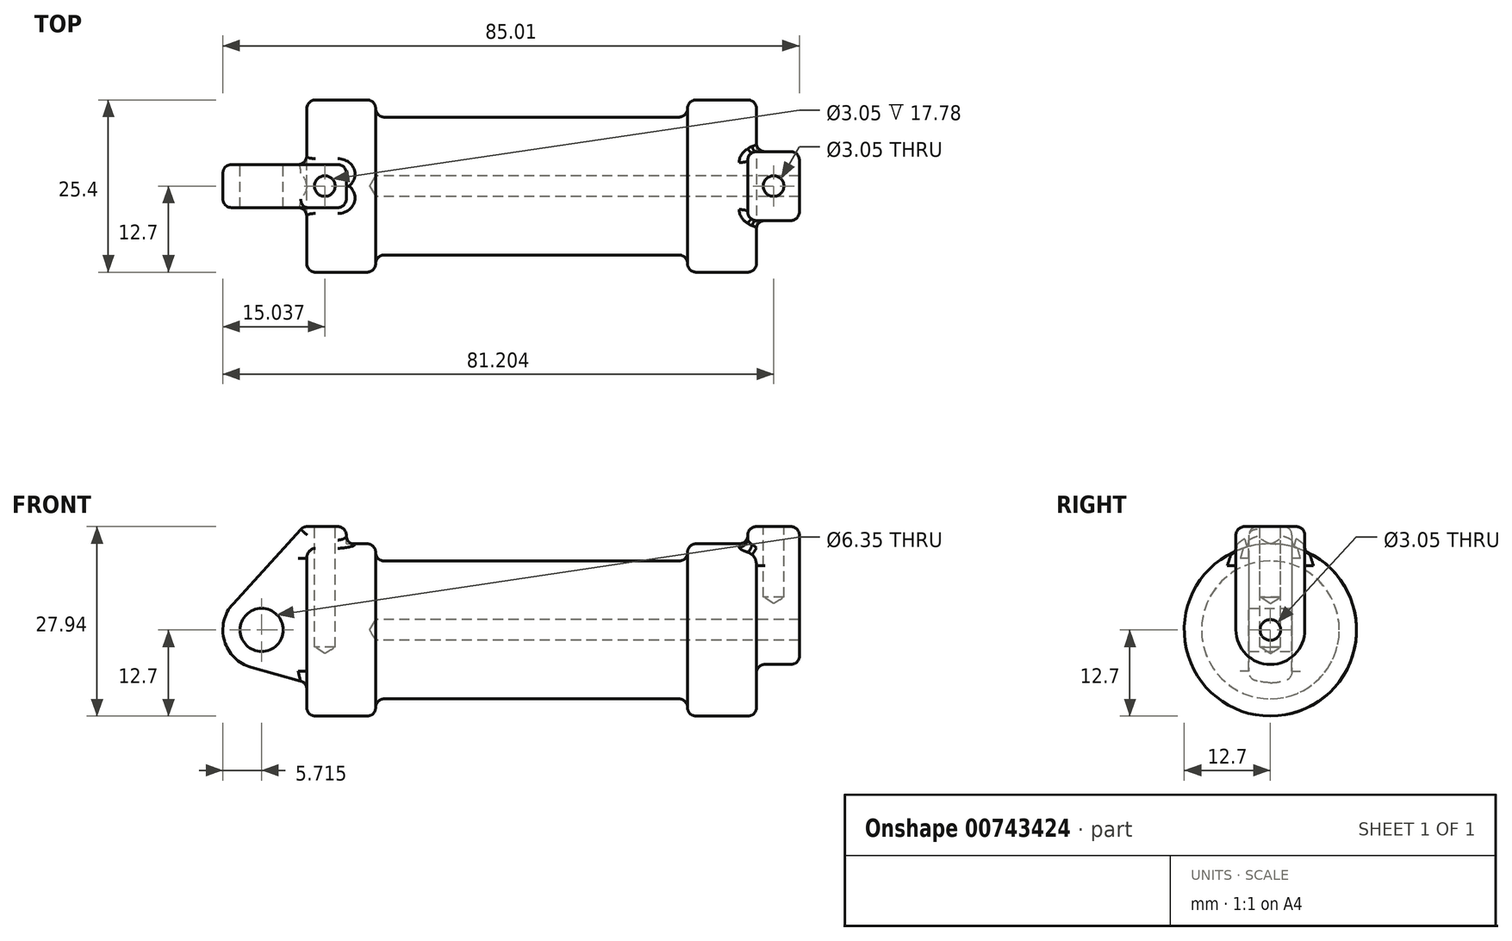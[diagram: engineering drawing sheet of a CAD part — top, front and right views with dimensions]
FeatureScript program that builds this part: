
annotation { "Feature Type Name" : "Feature", "Feature Type Description" : "" }
export const myFeature = defineFeature(function(context is Context, id is Id, definition is map)
    precondition{}
    {
        {
            var Q0;
            Q0=qCreatedBy(makeId("Front.planeOp"),FACE);
            var sketch = newSketch(context, id + "F0", { "sketchPlane" : qUnion([Q0])});
            skLineSegment(sketch, "E0", {"start": v(0, 0) * mm, "end": v(0, 12.7) * mm});
            skLineSegment(sketch, "E1", {"start": v(0, 12.7) * mm, "end": v(10.16, 12.7) * mm});
            skLineSegment(sketch, "E2", {"start": v(10.16, 12.7) * mm, "end": v(10.16, 10.16) * mm});
            skLineSegment(sketch, "E3", {"start": v(10.16, 10.16) * mm, "end": v(56.13, 10.16) * mm});
            skLineSegment(sketch, "E4", {"start": v(56.13, 10.16) * mm, "end": v(56.13, 12.7) * mm});
            skLineSegment(sketch, "E5", {"start": v(56.13, 12.7) * mm, "end": v(66.3, 12.7) * mm});
            skLineSegment(sketch, "E6", {"start": v(66.3, 12.7) * mm, "end": v(66.3, 0) * mm});
            skLineSegment(sketch, "E7", {"start": v(66.3, 0) * mm, "end": v(0, 0) * mm});
            skLineSegment(sketch, "E8", {"start": v(5.84, 15.24) * mm, "end": v(-0.5, 15.24) * mm});
            skLineSegment(sketch, "E9", {"start": v(-0.5, 15.24) * mm, "end": v(-10.88, 3.85) * mm});
            skLineSegment(sketch, "E10", {"start": v(0, 0) * mm, "end": v(-6.65, 0) * mm});
            skCircle(sketch, "E11", {"center": v(-6.65, 0) * mm, "radius": 5.72 * mm});
            skCircle(sketch, "E12", {"center": v(-6.65, 0) * mm, "radius": 3.18 * mm});
            skLineSegment(sketch, "E13", {"start": v(5.84, 15.24) * mm, "end": v(5.84, -9.4) * mm});
            skLineSegment(sketch, "E14", {"start": v(5.84, -9.4) * mm, "end": v(-8.18, -5.5) * mm});
            skSolve(sketch);
        }
        {
            var Q0;
            {var subQ0=sQuery(id+"F0.wireOp",EDGE,"E0");Q0=makeQuery(id+"F0.imprint","IMPRINT",FACE,{"disambiguationData":[TD([[makeQuery(id+"F0.imprint","IMPRINT",EDGE,{"derivedFrom":subQ0}),-1.0]])]});}
            var Q1;
            {var subQ0=sQuery(id+"F0.wireOp",EDGE,"E2");Q1=makeQuery(id+"F0.imprint","IMPRINT",FACE,{"disambiguationData":[TD([[makeQuery(id+"F0.imprint","IMPRINT",EDGE,{"derivedFrom":subQ0}),-1.0]])]});}
            var Q2;
            Q2=sQuery(id+"F0.wireOp",EDGE,"E7");
            revolve(context, id + "F1", {"surfaceOperationType" : NewSurfaceOperationType.NEW, "entities" : qUnion([Q0, Q1]), "axis" : qUnion([Q2]), "revolveType" : RevolveType.FULL});
        }
        {
            var Q0;
            {var subQ0=sQuery(id+"F0.wireOp",EDGE,"E14");Q0=makeQuery(id+"F0.imprint","IMPRINT",FACE,{"disambiguationData":[TD([[makeQuery(id+"F0.imprint","IMPRINT",EDGE,{"derivedFrom":subQ0}),-1.0]])]});}
            var Q1;
            {var subQ5=sQuery(id+"F0.wireOp",EDGE,"E12");Q1=makeQuery(id+"F0.imprint","IMPRINT",FACE,{"disambiguationData":[TD([[makeQuery(id+"F0.imprint","IMPRINT",EDGE,{"derivedFrom":subQ5}),-1.0]])]});}
            var Q2;
            {var subQ1=sQuery(id+"F0.wireOp",EDGE,"E0");Q2=makeQuery(id+"F0.imprint","IMPRINT",FACE,{"disambiguationData":[TD([[makeQuery(id+"F0.imprint","IMPRINT",EDGE,{"derivedFrom":subQ1}),1.0]])]});}
            var Q3;
            {var subQ0=sQuery(id+"F0.wireOp",EDGE,"E0");Q3=makeQuery(id+"F0.imprint","IMPRINT",FACE,{"disambiguationData":[TD([[makeQuery(id+"F0.imprint","IMPRINT",EDGE,{"derivedFrom":subQ0}),-1.0]])]});}
            extrude(context, id + "F2", {"entities" : qUnion([Q0, Q1, Q2, Q3]), "operationType" : NewBodyOperationType.ADD, "endBound" : BoundingType.SYMMETRIC, "depth" : 6.35 * mm, "offsetDistance" : 25.4 * mm});
        }
        {
            var Q0;
            Q0=makeQuery(id+"F1.opRevolve","SWEPT_FACE",FACE,{"disambiguationData":[OSD([sQuery(id+"F0.wireOp",EDGE,"E6")])]});
            var sketch = newSketch(context, id + "F3", { "sketchPlane" : qUnion([Q0])});
            skCircle(sketch, "E15", {"center": v(0, 0) * mm, "radius": 1.52 * mm});
            skCircle(sketch, "E16", {"center": v(0, 0) * mm, "radius": 5.08 * mm});
            skLineSegment(sketch, "E17", {"start": v(5.08, 0) * mm, "end": v(5.08, 15.24) * mm});
            skLineSegment(sketch, "E18", {"start": v(5.08, 15.24) * mm, "end": v(-5.08, 15.24) * mm});
            skLineSegment(sketch, "E19", {"start": v(-5.08, 15.24) * mm, "end": v(-5.08, 0) * mm});
            skSolve(sketch);
        }
        {
            var Q0;
            {var subQ0=sQuery(id+"F3.wireOp",EDGE,"E18");Q0=makeQuery(id+"F3.imprint","IMPRINT",FACE,{"disambiguationData":[TD([[makeQuery(id+"F3.imprint","IMPRINT",EDGE,{"derivedFrom":subQ0}),1.0]])]});}
            var Q1;
            {var subQ0=sQuery(id+"F3.wireOp",EDGE,"E17");var subQ1=sQuery(id+"F3.wireOp",EDGE,"E16");var subQ2=makeQuery(id+"F3.imprint","INTERSECT",VERTEX,{"derivedFrom":[subQ1,subQ0]});Q1=makeQuery(id+"F3.imprint","IMPRINT",FACE,{"disambiguationData":[TD([[makeQuery(id+"F3.imprint","IMPRINT",EDGE,{"disambiguationData":[TD([[subQ2,-1.0]])],"derivedFrom":subQ1}),-1.0]])]});}
            var Q2;
            Q2=makeQuery(id+"F3.imprint","IMPRINT",FACE,{"disambiguationData":[TD([[makeQuery(id+"F3.imprint","IMPRINT",EDGE,{"derivedFrom":sQuery(id+"F3.wireOp",EDGE,"E15")}),-1.0]])]});
            extrude(context, id + "F4", {"entities" : qUnion([Q0, Q1, Q2]), "operationType" : NewBodyOperationType.ADD, "depth" : 6.35 * mm, "offsetDistance" : 25.4 * mm, "hasSecondDirection" : true, "secondDirectionOppositeDirection" : true, "secondDirectionDepth" : 1.27 * mm});
        }
        {
            var Q0;
            Q0=sQuery(id+"F3.wireOp",VERTEX,"E15.center");
            var Q1;
            Q1=makeQuery(id+"F1.opRevolve","SWEPT_BODY",BODY,{"disambiguationData":[OSD([sQuery(id+"F0.wireOp",EDGE,"E0"),sQuery(id+"F0.wireOp",EDGE,"E1"),sQuery(id+"F0.wireOp",EDGE,"E2"),sQuery(id+"F0.wireOp",EDGE,"E3"),sQuery(id+"F0.wireOp",EDGE,"E4"),sQuery(id+"F0.wireOp",EDGE,"E5"),sQuery(id+"F0.wireOp",EDGE,"E6"),sQuery(id+"F0.wireOp",EDGE,"E7")])]});
            hole(context, id + "F5", {"style" : HoleStyle.SIMPLE, "endStyle" : HoleEndStyle.BLIND, "holeDiameter" : 3.05 * mm, "majorDiameter" : 6.35 * mm, "holeDepth" : 56.13 * mm, "isTappedThrough" : true, "tappedDepth" : 12.7 * mm, "tapClearance" : 3, "locations" : qUnion([Q0]), "scope" : qUnion([Q1])});
        }
        {
            var Q0;
            Q0=makeQuery(id+"F2.opExtrude","SWEPT_FACE",FACE,{"disambiguationData":[OSD([sQuery(id+"F0.wireOp",EDGE,"E8")])]});
            var sketch = newSketch(context, id + "F6", { "sketchPlane" : qUnion([Q0])});
            skLineSegment(sketch, "E20.0.0", {"start": v(65.02, 5.08) * mm, "end": v(65.02, -5.08) * mm});
            skLineSegment(sketch, "E20.0.1", {"start": v(65.02, -5.08) * mm, "end": v(72.64, -5.08) * mm});
            skLineSegment(sketch, "E20.0.2", {"start": v(72.64, -5.08) * mm, "end": v(72.64, 5.08) * mm});
            skLineSegment(sketch, "E20.0.3", {"start": v(72.64, 5.08) * mm, "end": v(65.02, 5.08) * mm});
            skLineSegment(sketch, "E21", {"start": v(-0.5, 0) * mm, "end": v(72.64, 0) * mm, "construction": true});
            skLineSegment(sketch, "E22", {"start": v(2.67, 3.18) * mm, "end": v(2.67, -3.18) * mm, "construction": true});
            skLineSegment(sketch, "E23", {"start": v(68.83, 5.08) * mm, "end": v(68.83, -5.08) * mm, "construction": true});
            skCircle(sketch, "E24", {"center": v(2.67, 0) * mm, "radius": 1.52 * mm});
            skCircle(sketch, "E25", {"center": v(68.83, 0) * mm, "radius": 1.52 * mm});
            skSolve(sketch);
        }
        {
            var Q0;
            Q0=sQuery(id+"F6.wireOp",VERTEX,"E24.center");
            var Q1;
            Q1=makeQuery(id+"F1.opRevolve","SWEPT_BODY",BODY,{"disambiguationData":[OSD([sQuery(id+"F0.wireOp",EDGE,"E0"),sQuery(id+"F0.wireOp",EDGE,"E1"),sQuery(id+"F0.wireOp",EDGE,"E2"),sQuery(id+"F0.wireOp",EDGE,"E3"),sQuery(id+"F0.wireOp",EDGE,"E4"),sQuery(id+"F0.wireOp",EDGE,"E5"),sQuery(id+"F0.wireOp",EDGE,"E6"),sQuery(id+"F0.wireOp",EDGE,"E7")])]});
            hole(context, id + "F7", {"style" : HoleStyle.SIMPLE, "endStyle" : HoleEndStyle.BLIND, "holeDiameter" : 3.05 * mm, "majorDiameter" : 6.35 * mm, "holeDepth" : 17.78 * mm, "isTappedThrough" : true, "tappedDepth" : 12.7 * mm, "tapClearance" : 3, "locations" : qUnion([Q0]), "scope" : qUnion([Q1])});
        }
        {
            var Q0;
            Q0=sQuery(id+"F6.wireOp",VERTEX,"E25.center");
            var Q1;
            Q1=makeQuery(id+"F1.opRevolve","SWEPT_BODY",BODY,{"disambiguationData":[OSD([sQuery(id+"F0.wireOp",EDGE,"E0"),sQuery(id+"F0.wireOp",EDGE,"E1"),sQuery(id+"F0.wireOp",EDGE,"E2"),sQuery(id+"F0.wireOp",EDGE,"E3"),sQuery(id+"F0.wireOp",EDGE,"E4"),sQuery(id+"F0.wireOp",EDGE,"E5"),sQuery(id+"F0.wireOp",EDGE,"E6"),sQuery(id+"F0.wireOp",EDGE,"E7")])]});
            hole(context, id + "F8", {"style" : HoleStyle.SIMPLE, "endStyle" : HoleEndStyle.BLIND, "holeDiameter" : 3.05 * mm, "majorDiameter" : 6.35 * mm, "holeDepth" : 10.4 * mm, "isTappedThrough" : true, "tappedDepth" : 12.7 * mm, "tapClearance" : 3, "locations" : qUnion([Q0]), "scope" : qUnion([Q1])});
        }
        {
            var Q0;
            Q0=makeQuery(id+"F1.opRevolve","SWEPT_EDGE",EDGE,{"disambiguationData":[OSD([sQuery(id+"F0.wireOp",EDGE,"E0"),sQuery(id+"F0.wireOp",EDGE,"E1")])]});
            var Q1;
            Q1=makeQuery(id+"F1.opRevolve","SWEPT_EDGE",EDGE,{"disambiguationData":[OSD([sQuery(id+"F0.wireOp",EDGE,"E1"),sQuery(id+"F0.wireOp",EDGE,"E2")])]});
            var Q2;
            Q2=makeQuery(id+"F1.opRevolve","SWEPT_EDGE",EDGE,{"disambiguationData":[OSD([sQuery(id+"F0.wireOp",EDGE,"E2"),sQuery(id+"F0.wireOp",EDGE,"E3")])]});
            var Q3;
            Q3=makeQuery(id+"F1.opRevolve","SWEPT_EDGE",EDGE,{"disambiguationData":[OSD([sQuery(id+"F0.wireOp",EDGE,"E4"),sQuery(id+"F0.wireOp",EDGE,"E5")])]});
            var Q4;
            Q4=makeQuery(id+"F1.opRevolve","SWEPT_EDGE",EDGE,{"disambiguationData":[OSD([sQuery(id+"F0.wireOp",EDGE,"E5"),sQuery(id+"F0.wireOp",EDGE,"E6")])]});
            var Q5;
            Q5=makeQuery(id+"F1.opRevolve","SWEPT_EDGE",EDGE,{"disambiguationData":[OSD([sQuery(id+"F0.wireOp",EDGE,"E3"),sQuery(id+"F0.wireOp",EDGE,"E4")])]});
            fillet(context, id + "F9", {"entities" : qUnion([Q0, Q1, Q2, Q3, Q4, Q5]), "radius" : 1.27 * mm, "tangentPropagation" : true, "allowEdgeOverflow" : false});
        }
        {
            var Q0;
            Q0=makeQuery(id+"F2.opExtrude","SWEPT_EDGE",EDGE,{"disambiguationData":[OSD([sQuery(id+"F0.wireOp",EDGE,"E8"),sQuery(id+"F0.wireOp",EDGE,"E13")])]});
            var Q1;
            Q1=makeQuery(id+"F2.opExtrude","CAP_EDGE",EDGE,{"disambiguationData":[OSD([sQuery(id+"F0.wireOp",EDGE,"E8")])],"isStart":false});
            var Q2;
            Q2=makeQuery(id+"F2.opExtrude","CAP_EDGE",EDGE,{"disambiguationData":[OSD([sQuery(id+"F0.wireOp",EDGE,"E9")])],"isStart":false});
            var Q3;
            Q3=makeQuery(id+"F2.boolean.opBoolean","INTERSECT",EDGE,{"derivedFrom":[makeQuery(id+"F1.opRevolve","SWEPT_FACE",FACE,{"disambiguationData":[OSD([sQuery(id+"F0.wireOp",EDGE,"E0")])]}),makeQuery(id+"F2.opExtrude","CAP_FACE",FACE,{"disambiguationData":[OSD([sQuery(id+"F0.wireOp",EDGE,"E8"),sQuery(id+"F0.wireOp",EDGE,"E9"),sQuery(id+"F0.wireOp",EDGE,"E11"),sQuery(id+"F0.wireOp",EDGE,"E12"),sQuery(id+"F0.wireOp",EDGE,"E13"),sQuery(id+"F0.wireOp",EDGE,"E14")])],"isStart":false})]});
            var Q4;
            Q4=makeQuery(id+"F2.opExtrude","CAP_EDGE",EDGE,{"disambiguationData":[OSD([sQuery(id+"F0.wireOp",EDGE,"E13")])],"isStart":false});
            fillet(context, id + "F10", {"entities" : qUnion([Q0, Q1, Q2, Q3, Q4]), "radius" : 1.27 * mm, "tangentPropagation" : true, "allowEdgeOverflow" : false});
        }
        {
            var Q0;
            Q0=makeQuery(id+"F2.opExtrude","CAP_EDGE",EDGE,{"disambiguationData":[OSD([sQuery(id+"F0.wireOp",EDGE,"E11")])],"isStart":true});
            var Q1;
            Q1=makeQuery(id+"F2.opExtrude","SWEPT_EDGE",EDGE,{"disambiguationData":[OSD([sQuery(id+"F0.wireOp",EDGE,"E8"),sQuery(id+"F0.wireOp",EDGE,"E9")])]});
            var Q2;
            Q2=makeQuery(id+"F2.boolean.opBoolean","INTERSECT",EDGE,{"derivedFrom":[makeQuery(id+"F1.opRevolve","SWEPT_FACE",FACE,{"disambiguationData":[OSD([sQuery(id+"F0.wireOp",EDGE,"E0")])]}),makeQuery(id+"F2.opExtrude","CAP_FACE",FACE,{"disambiguationData":[OSD([sQuery(id+"F0.wireOp",EDGE,"E8"),sQuery(id+"F0.wireOp",EDGE,"E9"),sQuery(id+"F0.wireOp",EDGE,"E11"),sQuery(id+"F0.wireOp",EDGE,"E12"),sQuery(id+"F0.wireOp",EDGE,"E13"),sQuery(id+"F0.wireOp",EDGE,"E14")])],"isStart":true})]});
            var Q3;
            Q3=makeQuery(id+"F2.opExtrude","CAP_EDGE",EDGE,{"disambiguationData":[OSD([sQuery(id+"F0.wireOp",EDGE,"E13")])],"isStart":true});
            fillet(context, id + "F11", {"entities" : qUnion([Q0, Q1, Q2, Q3]), "radius" : 1.27 * mm, "tangentPropagation" : true, "allowEdgeOverflow" : false});
        }
        {
            var Q0;
            Q0=makeQuery(id+"F4.boolean.opBoolean","INTERSECT",EDGE,{"derivedFrom":[makeQuery(id+"F1.opRevolve","SWEPT_FACE",FACE,{"disambiguationData":[OSD([sQuery(id+"F0.wireOp",EDGE,"E6")])]}),makeQuery(id+"F4.opExtrude","SWEPT_FACE",FACE,{"disambiguationData":[OSD([sQuery(id+"F3.wireOp",EDGE,"E19")])]})]});
            var Q1;
            Q1=makeQuery(id+"F4.opExtrude","SWEPT_EDGE",EDGE,{"disambiguationData":[OSD([sQuery(id+"F3.wireOp",EDGE,"E18"),sQuery(id+"F3.wireOp",EDGE,"E19")])]});
            var Q2;
            Q2=makeQuery(id+"F4.opExtrude","SWEPT_EDGE",EDGE,{"disambiguationData":[OSD([sQuery(id+"F3.wireOp",EDGE,"E17"),sQuery(id+"F3.wireOp",EDGE,"E18")])]});
            var Q3;
            Q3=makeQuery(id+"F4.opExtrude","CAP_EDGE",EDGE,{"disambiguationData":[OSD([sQuery(id+"F3.wireOp",EDGE,"E18")])],"isStart":true});
            var Q4;
            Q4=makeQuery(id+"F4.opExtrude","CAP_EDGE",EDGE,{"disambiguationData":[OSD([sQuery(id+"F3.wireOp",EDGE,"E19")])],"isStart":false});
            var Q5;
            Q5=makeQuery(id+"F4.boolean.opBoolean","INTERSECT",EDGE,{"derivedFrom":[makeQuery(id+"F1.opRevolve","SWEPT_FACE",FACE,{"disambiguationData":[OSD([sQuery(id+"F0.wireOp",EDGE,"E5")])]}),makeQuery(id+"F4.opExtrude","CAP_FACE",FACE,{"disambiguationData":[OSD([sQuery(id+"F3.wireOp",EDGE,"E15"),sQuery(id+"F3.wireOp",EDGE,"E16"),sQuery(id+"F3.wireOp",EDGE,"E17"),sQuery(id+"F3.wireOp",EDGE,"E18"),sQuery(id+"F3.wireOp",EDGE,"E19")])],"isStart":true})]});
            var Q6;
            Q6=makeQuery(id+"F4.opExtrude","CAP_EDGE",EDGE,{"disambiguationData":[OSD([sQuery(id+"F3.wireOp",EDGE,"E17")])],"isStart":true});
            var Q7;
            Q7=makeQuery(id+"F4.opExtrude","CAP_EDGE",EDGE,{"disambiguationData":[OSD([sQuery(id+"F3.wireOp",EDGE,"E19")])],"isStart":true});
            var Q8;
            Q8=makeQuery(id+"F4.opExtrude","CAP_EDGE",EDGE,{"disambiguationData":[OSD([sQuery(id+"F3.wireOp",EDGE,"E18")])],"isStart":false});
            fillet(context, id + "F12", {"entities" : qUnion([Q0, Q1, Q2, Q3, Q4, Q5, Q6, Q7, Q8]), "radius" : 1.27 * mm, "tangentPropagation" : true, "allowEdgeOverflow" : false});
        }
    });
